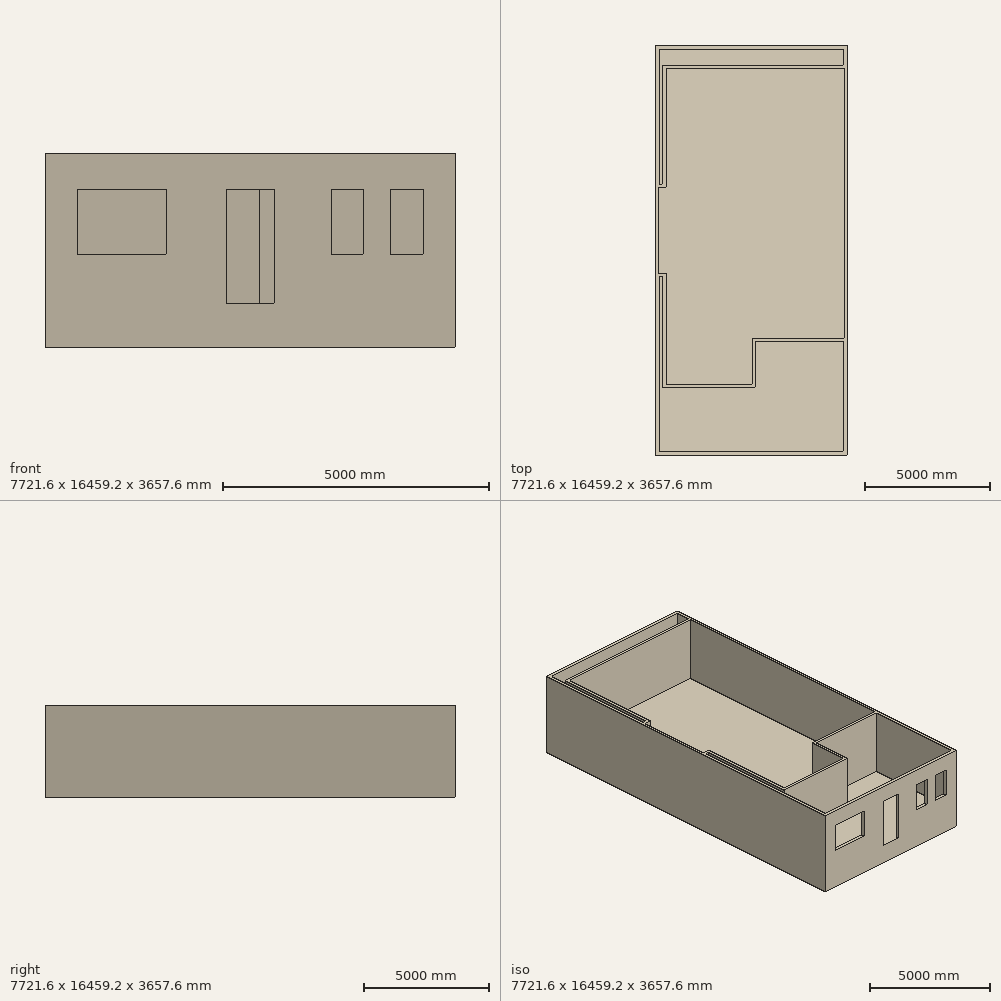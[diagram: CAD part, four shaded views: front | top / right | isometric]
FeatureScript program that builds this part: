
annotation { "Feature Type Name" : "Feature", "Feature Type Description" : "" }
export const myFeature = defineFeature(function(context is Context, id is Id, definition is map)
    precondition{}
    {
        {
            var Q0;
            Q0=qCreatedBy(makeId("Top.planeOp"),FACE);
            var sketch = newSketch(context, id + "F0", { "sketchPlane" : qUnion([Q0])});
            skLineSegment(sketch, "E0", {"start": v(3683, 0) * mm, "end": v(3683, 11099.8) * mm});
            skLineSegment(sketch, "E1", {"start": v(3683, 11099.8) * mm, "end": v(-3733.8, 11099.8) * mm});
            skLineSegment(sketch, "E2", {"start": v(-3733.8, 11099.8) * mm, "end": v(-3733.8, 6324.6) * mm});
            skLineSegment(sketch, "E3", {"start": v(-3733.8, 6324.6) * mm, "end": v(-4038.6, 6324.6) * mm});
            skLineSegment(sketch, "E4", {"start": v(-4038.6, 6324.6) * mm, "end": v(-4038.6, 2616.2) * mm});
            skLineSegment(sketch, "E5", {"start": v(-4038.6, 2616.2) * mm, "end": v(-3733.8, 2616.2) * mm});
            skLineSegment(sketch, "E6", {"start": v(-3733.8, 2616.2) * mm, "end": v(-3733.8, -1828.8) * mm});
            skLineSegment(sketch, "E7", {"start": v(0, -1828.8) * mm, "end": v(0, 0) * mm});
            skLineSegment(sketch, "E8", {"start": v(0, 0) * mm, "end": v(3683, 0) * mm});
            skPoint(sketch, "E9.orphan", {"position": v(3683, 0) * mm});
            skLineSegment(sketch, "E10", {"start": v(-3733.8, -1828.8) * mm, "end": v(0, -1828.8) * mm});
            skLineSegment(sketch, "E11.0", {"start": v(-127, -1701.8) * mm, "end": v(-127, 127) * mm});
            skLineSegment(sketch, "E11.1", {"start": v(-3606.8, -1701.8) * mm, "end": v(-127, -1701.8) * mm});
            skLineSegment(sketch, "E11.2", {"start": v(-3606.8, 2743.2) * mm, "end": v(-3606.8, -1701.8) * mm});
            skLineSegment(sketch, "E11.3", {"start": v(-3911.6, 2743.2) * mm, "end": v(-3606.8, 2743.2) * mm});
            skLineSegment(sketch, "E11.4", {"start": v(-3911.6, 6197.6) * mm, "end": v(-3911.6, 2743.2) * mm});
            skLineSegment(sketch, "E11.5", {"start": v(-127, 127) * mm, "end": v(3556, 127) * mm});
            skLineSegment(sketch, "E11.6", {"start": v(-3606.8, 6197.6) * mm, "end": v(-3911.6, 6197.6) * mm});
            skLineSegment(sketch, "E11.7", {"start": v(-3606.8, 10972.8) * mm, "end": v(-3606.8, 6197.6) * mm});
            skLineSegment(sketch, "E11.8", {"start": v(3556, 10972.8) * mm, "end": v(-3606.8, 10972.8) * mm});
            skLineSegment(sketch, "E11.9", {"start": v(3556, 127) * mm, "end": v(3556, 10972.8) * mm});
            skLineSegment(sketch, "E12.bottom", {"start": v(-3746.5, 438.15) * mm, "end": v(-3594.1, 438.15) * mm, "construction": true});
            skLineSegment(sketch, "E12.top", {"start": v(-3746.5, 1352.55) * mm, "end": v(-3594.1, 1352.55) * mm, "construction": true});
            skLineSegment(sketch, "E12.left", {"start": v(-3746.5, 438.15) * mm, "end": v(-3746.5, 1352.55) * mm, "construction": true});
            skLineSegment(sketch, "E12.right", {"start": v(-3594.1, 438.15) * mm, "end": v(-3594.1, 1352.55) * mm, "construction": true});
            skLineSegment(sketch, "E13", {"start": v(-3606.8, 2609.85) * mm, "end": v(-2933.7, 2609.85) * mm, "construction": true});
            skLineSegment(sketch, "E14", {"start": v(-2933.7, 2609.85) * mm, "end": v(-2933.7, 2743.2) * mm, "construction": true});
            skLineSegment(sketch, "E15", {"start": v(-2933.7, 2743.2) * mm, "end": v(-3606.8, 2743.2) * mm, "construction": true});
            skLineSegment(sketch, "E16.bottom", {"start": v(-2705.1, -1689.1) * mm, "end": v(-1054.1, -1689.1) * mm, "construction": true});
            skLineSegment(sketch, "E16.top", {"start": v(-2705.1, -1841.5) * mm, "end": v(-1054.1, -1841.5) * mm, "construction": true});
            skLineSegment(sketch, "E16.left", {"start": v(-2705.1, -1689.1) * mm, "end": v(-2705.1, -1841.5) * mm, "construction": true});
            skLineSegment(sketch, "E16.right", {"start": v(-1054.1, -1689.1) * mm, "end": v(-1054.1, -1841.5) * mm, "construction": true});
            skLineSegment(sketch, "E17", {"start": v(-127, 127) * mm, "end": v(-127, 2609.85) * mm, "construction": true});
            skLineSegment(sketch, "E18", {"start": v(-127, 2609.85) * mm, "end": v(-800.1, 2609.85) * mm, "construction": true});
            skLineSegment(sketch, "E19", {"start": v(-800.1, 2743.2) * mm, "end": v(-88.9, 2743.2) * mm, "construction": true});
            skLineSegment(sketch, "E20", {"start": v(-88.9, 2743.2) * mm, "end": v(660.4, 3359.05) * mm, "construction": true});
            skLineSegment(sketch, "E21", {"start": v(660.4, 3359.05) * mm, "end": v(660.4, 5268.85) * mm, "construction": true});
            skLineSegment(sketch, "E22", {"start": v(0, 127) * mm, "end": v(0, 2680.36) * mm, "construction": true});
            skLineSegment(sketch, "E23", {"start": v(76.33, 2747.5) * mm, "end": v(800.1, 1866.9) * mm, "construction": true});
            skLineSegment(sketch, "E24", {"start": v(800.1, 1866.9) * mm, "end": v(800.1, 127) * mm, "construction": true});
            skLineSegment(sketch, "E25", {"start": v(-800.1, 2743.2) * mm, "end": v(-800.1, 2609.85) * mm});
            skLineSegment(sketch, "E26", {"start": v(76.33, 2747.5) * mm, "end": v(812.8, 3352.8) * mm, "construction": true});
            skLineSegment(sketch, "E27", {"start": v(812.8, 3352.8) * mm, "end": v(3556, 3352.8) * mm, "construction": true});
            skLineSegment(sketch, "E28", {"start": v(3556, 3479.8) * mm, "end": v(787.4, 3479.8) * mm, "construction": true});
            skLineSegment(sketch, "E29", {"start": v(787.4, 3479.8) * mm, "end": v(787.4, 5181.6) * mm, "construction": true});
            skLineSegment(sketch, "E30", {"start": v(787.4, 5181.6) * mm, "end": v(3556, 5181.6) * mm, "construction": true});
            skLineSegment(sketch, "E31", {"start": v(3541.89, 5308.6) * mm, "end": v(781.97, 5308.6) * mm, "construction": true});
            skLineSegment(sketch, "E32", {"start": v(781.97, 5308.6) * mm, "end": v(0, 5845.85) * mm, "construction": true});
            skLineSegment(sketch, "E33", {"start": v(0, 8534.4) * mm, "end": v(698.5, 8534.4) * mm, "construction": true});
            skLineSegment(sketch, "E34", {"start": v(660.4, 5268.85) * mm, "end": v(-293.97, 5924.55) * mm, "construction": true});
            skLineSegment(sketch, "E35", {"start": v(-293.97, 5924.55) * mm, "end": v(-293.97, 6197.6) * mm, "construction": true});
            skLineSegment(sketch, "E36", {"start": v(-293.97, 6197.6) * mm, "end": v(-3606.8, 6197.6) * mm, "construction": true});
            skLineSegment(sketch, "E37.bottom", {"start": v(1346.2, 139.7) * mm, "end": v(2070.1, 139.7) * mm, "construction": true});
            skLineSegment(sketch, "E37.top", {"start": v(1346.2, -12.7) * mm, "end": v(2070.1, -12.7) * mm, "construction": true});
            skLineSegment(sketch, "E37.left", {"start": v(1346.2, 139.7) * mm, "end": v(1346.2, -12.7) * mm, "construction": true});
            skLineSegment(sketch, "E37.right", {"start": v(2070.1, 139.7) * mm, "end": v(2070.1, -12.7) * mm, "construction": true});
            skLineSegment(sketch, "E38.bottom", {"start": v(3543.3, 2781.3) * mm, "end": v(3695.7, 2781.3) * mm, "construction": true});
            skLineSegment(sketch, "E38.top", {"start": v(3543.3, 2051.05) * mm, "end": v(3695.7, 2051.05) * mm, "construction": true});
            skLineSegment(sketch, "E38.left", {"start": v(3543.3, 2781.3) * mm, "end": v(3543.3, 2051.05) * mm, "construction": true});
            skLineSegment(sketch, "E38.right", {"start": v(3695.7, 2781.3) * mm, "end": v(3695.7, 2051.05) * mm, "construction": true});
            skLineSegment(sketch, "E39", {"start": v(0, 2680.36) * mm, "end": v(698.5, 1830.5) * mm, "construction": true});
            skLineSegment(sketch, "E40", {"start": v(698.5, 1830.5) * mm, "end": v(698.5, 127) * mm, "construction": true});
            skLineSegment(sketch, "E41.bottom", {"start": v(3543.3, 4610.1) * mm, "end": v(3695.7, 4610.1) * mm, "construction": true});
            skLineSegment(sketch, "E41.top", {"start": v(3543.3, 4038.6) * mm, "end": v(3695.7, 4038.6) * mm, "construction": true});
            skLineSegment(sketch, "E41.left", {"start": v(3543.3, 4610.1) * mm, "end": v(3543.3, 4038.6) * mm, "construction": true});
            skLineSegment(sketch, "E41.right", {"start": v(3695.7, 4610.1) * mm, "end": v(3695.7, 4038.6) * mm, "construction": true});
            skLineSegment(sketch, "E42.bottom", {"start": v(635, 4394.2) * mm, "end": v(787.4, 4394.2) * mm, "construction": true});
            skLineSegment(sketch, "E42.top", {"start": v(635, 3632.2) * mm, "end": v(787.4, 3632.2) * mm, "construction": true});
            skLineSegment(sketch, "E42.left", {"start": v(635, 4394.2) * mm, "end": v(635, 3632.2) * mm, "construction": true});
            skLineSegment(sketch, "E42.right", {"start": v(787.4, 4394.2) * mm, "end": v(787.4, 3632.2) * mm, "construction": true});
            skLineSegment(sketch, "E43.bottom", {"start": v(-427.32, 6172.2) * mm, "end": v(-1189.32, 6172.2) * mm, "construction": true});
            skLineSegment(sketch, "E43.top", {"start": v(-427.32, 6324.6) * mm, "end": v(-1189.32, 6324.6) * mm, "construction": true});
            skLineSegment(sketch, "E43.left", {"start": v(-427.32, 6172.2) * mm, "end": v(-427.32, 6324.6) * mm, "construction": true});
            skLineSegment(sketch, "E43.right", {"start": v(-1189.32, 6172.2) * mm, "end": v(-1189.32, 6324.6) * mm, "construction": true});
            skLineSegment(sketch, "E44.bottom", {"start": v(-4064, 3619.5) * mm, "end": v(-3911.6, 3619.5) * mm, "construction": true});
            skLineSegment(sketch, "E44.top", {"start": v(-4064, 4349.75) * mm, "end": v(-3911.6, 4349.75) * mm, "construction": true});
            skLineSegment(sketch, "E44.left", {"start": v(-4064, 3619.5) * mm, "end": v(-4064, 4349.75) * mm, "construction": true});
            skLineSegment(sketch, "E44.right", {"start": v(-3911.6, 3619.5) * mm, "end": v(-3911.6, 4349.75) * mm, "construction": true});
            skLineSegment(sketch, "E45.bottom", {"start": v(3543.3, 5867.4) * mm, "end": v(3695.7, 5867.4) * mm, "construction": true});
            skLineSegment(sketch, "E45.top", {"start": v(3543.3, 7061.2) * mm, "end": v(3695.7, 7061.2) * mm, "construction": true});
            skLineSegment(sketch, "E45.left", {"start": v(3543.3, 5867.4) * mm, "end": v(3543.3, 7061.2) * mm, "construction": true});
            skLineSegment(sketch, "E45.right", {"start": v(3695.7, 5867.4) * mm, "end": v(3695.7, 7061.2) * mm, "construction": true});
            skLineSegment(sketch, "E46.bottom", {"start": v(3543.3, 9438.28) * mm, "end": v(3695.7, 9438.28) * mm, "construction": true});
            skLineSegment(sketch, "E46.top", {"start": v(3543.3, 10256.66) * mm, "end": v(3695.7, 10256.66) * mm, "construction": true});
            skLineSegment(sketch, "E46.left", {"start": v(3543.3, 9438.28) * mm, "end": v(3543.3, 10256.66) * mm, "construction": true});
            skLineSegment(sketch, "E46.right", {"start": v(3695.7, 9438.28) * mm, "end": v(3695.7, 10256.66) * mm, "construction": true});
            skLineSegment(sketch, "E47.bottom", {"start": v(2881.46, 10778.72) * mm, "end": v(1984.95, 10778.72) * mm, "construction": true});
            skLineSegment(sketch, "E47.top", {"start": v(2881.46, 10931.12) * mm, "end": v(1984.95, 10931.12) * mm, "construction": true});
            skLineSegment(sketch, "E47.left", {"start": v(2881.46, 10778.72) * mm, "end": v(2881.46, 10931.12) * mm, "construction": true});
            skLineSegment(sketch, "E47.right", {"start": v(1984.95, 10778.72) * mm, "end": v(1984.95, 10931.12) * mm, "construction": true});
            skLineSegment(sketch, "E48.bottom", {"start": v(1766.71, 10778.72) * mm, "end": v(966.52, 10778.72) * mm, "construction": true});
            skLineSegment(sketch, "E48.top", {"start": v(1766.71, 10931.12) * mm, "end": v(966.52, 10931.12) * mm, "construction": true});
            skLineSegment(sketch, "E48.left", {"start": v(1766.71, 10778.72) * mm, "end": v(1766.71, 10931.12) * mm, "construction": true});
            skLineSegment(sketch, "E48.right", {"start": v(966.52, 10778.72) * mm, "end": v(966.52, 10931.12) * mm, "construction": true});
            skLineSegment(sketch, "E49.bottom", {"start": v(-1415.88, 10778.72) * mm, "end": v(-2525.25, 10778.72) * mm, "construction": true});
            skLineSegment(sketch, "E49.top", {"start": v(-1415.88, 10931.12) * mm, "end": v(-2525.25, 10931.12) * mm, "construction": true});
            skLineSegment(sketch, "E49.left", {"start": v(-1415.88, 10778.72) * mm, "end": v(-1415.88, 10931.12) * mm, "construction": true});
            skLineSegment(sketch, "E49.right", {"start": v(-2525.25, 10778.72) * mm, "end": v(-2525.25, 10931.12) * mm, "construction": true});
            skPoint(sketch, "E50.oppositeSnap0", {"position": v(-3606.8, 8585.2) * mm});
            skLineSegment(sketch, "E50.bottom", {"start": v(-3936.87, 7828.6) * mm, "end": v(-4089.27, 7828.6) * mm, "construction": true});
            skLineSegment(sketch, "E50.top", {"start": v(-3936.87, 8585.2) * mm, "end": v(-4089.27, 8585.2) * mm, "construction": true});
            skLineSegment(sketch, "E50.left", {"start": v(-3936.87, 7828.6) * mm, "end": v(-3936.87, 8585.2) * mm, "construction": true});
            skLineSegment(sketch, "E50.right", {"start": v(-4089.27, 7828.6) * mm, "end": v(-4089.27, 8585.2) * mm, "construction": true});
            skLineSegment(sketch, "E51", {"start": v(-3606.8, 6299.2) * mm, "end": v(-293.97, 6299.2) * mm, "construction": true});
            skLineSegment(sketch, "E52", {"start": v(-293.97, 6299.2) * mm, "end": v(-293.97, 9093.2) * mm, "construction": true});
            skLineSegment(sketch, "E53", {"start": v(-293.97, 9093.2) * mm, "end": v(-805.07, 9093.2) * mm, "construction": true});
            skLineSegment(sketch, "E54", {"start": v(-805.07, 9093.2) * mm, "end": v(-805.07, 9245.6) * mm, "construction": true});
            skLineSegment(sketch, "E55", {"start": v(-805.07, 9245.6) * mm, "end": v(-293.97, 9245.6) * mm, "construction": true});
            skLineSegment(sketch, "E56", {"start": v(-293.97, 9245.6) * mm, "end": v(-293.97, 10972.8) * mm, "construction": true});
            skLineSegment(sketch, "E57", {"start": v(-107.65, 5765.72) * mm, "end": v(520.4, 5334.22) * mm, "construction": true});
            skLineSegment(sketch, "E58", {"start": v(520.4, 5334.22) * mm, "end": v(606.7, 5459.83) * mm, "construction": true});
            skLineSegment(sketch, "E59", {"start": v(606.7, 5459.83) * mm, "end": v(-21.35, 5891.33) * mm, "construction": true});
            skLineSegment(sketch, "E60", {"start": v(-21.35, 5891.33) * mm, "end": v(-107.65, 5765.72) * mm, "construction": true});
            skLineSegment(sketch, "E61", {"start": v(50.34, 2893.8) * mm, "end": v(639.02, 3377.65) * mm, "construction": true});
            skLineSegment(sketch, "E62", {"start": v(639.02, 3377.65) * mm, "end": v(735.79, 3259.91) * mm, "construction": true});
            skLineSegment(sketch, "E63", {"start": v(735.79, 3259.91) * mm, "end": v(147.1, 2776.07) * mm, "construction": true});
            skLineSegment(sketch, "E64", {"start": v(147.1, 2776.07) * mm, "end": v(50.34, 2893.8) * mm, "construction": true});
            skLineSegment(sketch, "E65", {"start": v(800.1, 8534.4) * mm, "end": v(800.1, 7010.4) * mm, "construction": true});
            skLineSegment(sketch, "E66", {"start": v(800.1, 7010.4) * mm, "end": v(0, 5845.85) * mm, "construction": true});
            skLineSegment(sketch, "E67", {"start": v(0, 6025.27) * mm, "end": v(698.5, 7041.94) * mm, "construction": true});
            skLineSegment(sketch, "E68", {"start": v(698.5, 7041.94) * mm, "end": v(698.5, 8534.4) * mm, "construction": true});
            skLineSegment(sketch, "E69.bottom", {"start": v(-4064, 4527.55) * mm, "end": v(-3911.6, 4527.55) * mm, "construction": true});
            skLineSegment(sketch, "E69.top", {"start": v(-4064, 5257.8) * mm, "end": v(-3911.6, 5257.8) * mm, "construction": true});
            skLineSegment(sketch, "E69.left", {"start": v(-4064, 4527.55) * mm, "end": v(-4064, 5257.8) * mm, "construction": true});
            skLineSegment(sketch, "E69.right", {"start": v(-3911.6, 4527.55) * mm, "end": v(-3911.6, 5257.8) * mm, "construction": true});
            skLineSegment(sketch, "E70.trimOffspring", {"start": v(800.1, 8534.4) * mm, "end": v(3556, 8534.4) * mm, "construction": true});
            skLineSegment(sketch, "E71", {"start": v(0, 8686.8) * mm, "end": v(3556, 8686.8) * mm, "construction": true});
            skLineSegment(sketch, "E72.trimOffspring", {"start": v(0, 6025.27) * mm, "end": v(0, 8534.4) * mm, "construction": true});
            skLineSegment(sketch, "E73.trimOffspring", {"start": v(0, 8686.8) * mm, "end": v(0, 10972.8) * mm, "construction": true});
            skSolve(sketch);
        }
        {
            var Q0;
            Q0 = qSketchRegion(id + "F0", true);
            extrude(context, id + "F1", {"entities" : qUnion([Q0]), "depth" : 3657.6 * mm});
        }
        {
            var Q0;
            Q0=qCreatedBy(makeId("Top.planeOp"),FACE);
            var sketch = newSketch(context, id + "F2", { "sketchPlane" : qUnion([Q0])});
            skLineSegment(sketch, "E74.bottom", {"start": v(3683, -4572) * mm, "end": v(-4038.6, -4572) * mm});
            skLineSegment(sketch, "E74.top", {"start": v(3683, 11887.2) * mm, "end": v(-4038.6, 11887.2) * mm});
            skLineSegment(sketch, "E74.left", {"start": v(3683, -4572) * mm, "end": v(3683, 0) * mm});
            skLineSegment(sketch, "E74.right", {"start": v(-4038.6, -4572) * mm, "end": v(-4038.6, 2616.2) * mm});
            skLineSegment(sketch, "E75.0", {"start": v(3530.6, 11734.8) * mm, "end": v(-3886.2, 11734.8) * mm});
            skLineSegment(sketch, "E75.1", {"start": v(-3886.2, -4419.6) * mm, "end": v(-3886.2, 2616.2) * mm});
            skLineSegment(sketch, "E75.2", {"start": v(3530.6, -4419.6) * mm, "end": v(-3886.2, -4419.6) * mm});
            skLineSegment(sketch, "E75.3", {"start": v(3530.6, -4419.6) * mm, "end": v(3530.6, 0) * mm});
            skLineSegment(sketch, "E76", {"start": v(3530.6, 0) * mm, "end": v(3683, 0) * mm});
            skLineSegment(sketch, "E77", {"start": v(-4038.6, 2616.2) * mm, "end": v(-3886.2, 2616.2) * mm});
            skLineSegment(sketch, "E78", {"start": v(-4038.6, 6324.6) * mm, "end": v(-3886.2, 6324.6) * mm});
            skLineSegment(sketch, "E79.trimOffspring", {"start": v(-3886.2, 6324.6) * mm, "end": v(-3886.2, 11734.8) * mm});
            skLineSegment(sketch, "E80.trimOffspring", {"start": v(-4038.6, 6324.6) * mm, "end": v(-4038.6, 11887.2) * mm});
            skLineSegment(sketch, "E81", {"start": v(3683, 11887.2) * mm, "end": v(3683, 11099.8) * mm});
            skLineSegment(sketch, "E82", {"start": v(3683, 11099.8) * mm, "end": v(3530.6, 11099.8) * mm});
            skLineSegment(sketch, "E83", {"start": v(3530.6, 11099.8) * mm, "end": v(3530.6, 11734.8) * mm});
            skSolve(sketch);
        }
        {
            var Q0;
            Q0 = qSketchRegion(id + "F2", true);
            extrude(context, id + "F3", {"entities" : qUnion([Q0]), "operationType" : NewBodyOperationType.ADD, "depth" : 762 * mm});
        }
        {
            var Q0;
            Q0=makeQuery(id+"F3.opExtrude","CAP_FACE",FACE,{"disambiguationData":[OSD([sQuery(id+"F2.wireOp",EDGE,"E74.bottom"),sQuery(id+"F2.wireOp",EDGE,"E74.left"),sQuery(id+"F2.wireOp",EDGE,"E74.right"),sQuery(id+"F2.wireOp",EDGE,"E75.1"),sQuery(id+"F2.wireOp",EDGE,"E75.2"),sQuery(id+"F2.wireOp",EDGE,"E75.3"),sQuery(id+"F2.wireOp",EDGE,"E76"),sQuery(id+"F2.wireOp",EDGE,"E77")])],"isStart":false});
            var sketch = newSketch(context, id + "F4", { "sketchPlane" : qUnion([Q0])});
            skLineSegment(sketch, "E84.0", {"start": v(3683, -4572) * mm, "end": v(3683, 0) * mm});
            skLineSegment(sketch, "E85.0", {"start": v(3683, -4572) * mm, "end": v(-4038.6, -4572) * mm});
            skLineSegment(sketch, "E86.1", {"start": v(-4038.6, -4572) * mm, "end": v(-4038.6, 2616.2) * mm});
            skLineSegment(sketch, "E87.2", {"start": v(-4038.6, 6324.6) * mm, "end": v(-4038.6, 2616.2) * mm});
            skLineSegment(sketch, "E88.3", {"start": v(-4038.6, 6324.6) * mm, "end": v(-4038.6, 11887.2) * mm});
            skLineSegment(sketch, "E89.4", {"start": v(3683, 11887.2) * mm, "end": v(-4038.6, 11887.2) * mm});
            skLineSegment(sketch, "E89.5", {"start": v(3683, 0) * mm, "end": v(3683, 11099.8) * mm});
            skLineSegment(sketch, "E90.0", {"start": v(3683, 11887.2) * mm, "end": v(3683, 11099.8) * mm});
            skSolve(sketch);
        }
        {
            var Q0;
            Q0 = qSketchRegion(id + "F4", true);
            extrude(context, id + "F5", {"entities" : qUnion([Q0]), "operationType" : NewBodyOperationType.ADD, "depth" : 76.2 * mm});
        }
        {
            var Q0;
            {var subQ0=sQuery(id+"F4.wireOp",EDGE,"E84.0");var subQ1=sQuery(id+"F4.wireOp",EDGE,"E85.0");var subQ2=sQuery(id+"F4.wireOp",EDGE,"E86.1");var subQ3=sQuery(id+"F4.wireOp",EDGE,"E87.2");var subQ4=sQuery(id+"F4.wireOp",EDGE,"E88.3");var subQ5=sQuery(id+"F4.wireOp",EDGE,"E89.5");var subQ6=sQuery(id+"F4.wireOp",EDGE,"E90.0");Q0=makeQuery(id+"F5.boolean.opBoolean","SPLIT",FACE,{"disambiguationData":[TD([makeQuery(id+"F1.opExtrude","SWEPT_FACE",FACE,{"disambiguationData":[OSD([sQuery(id+"F0.wireOp",EDGE,"E5")])]})])],"derivedFrom":makeQuery(id+"F5.opExtrude","CAP_FACE",FACE,{"disambiguationData":[OSD([subQ0,subQ1,subQ2,subQ3,subQ4,sQuery(id+"F4.wireOp",EDGE,"E89.4"),subQ5,subQ6])],"isStart":false})});}
            var sketch = newSketch(context, id + "F6", { "sketchPlane" : qUnion([Q0])});
            skLineSegment(sketch, "E91.0", {"start": v(3683, -4572) * mm, "end": v(-4038.6, -4572) * mm});
            skLineSegment(sketch, "E91.1", {"start": v(3683, 11887.2) * mm, "end": v(-4038.6, 11887.2) * mm});
            skLineSegment(sketch, "E91.2", {"start": v(3683, -4572) * mm, "end": v(3683, 0) * mm});
            skLineSegment(sketch, "E91.3", {"start": v(-4038.6, -4572) * mm, "end": v(-4038.6, 2616.2) * mm});
            skLineSegment(sketch, "E91.4", {"start": v(3530.6, 11734.8) * mm, "end": v(-3886.2, 11734.8) * mm});
            skLineSegment(sketch, "E91.5", {"start": v(-3886.2, -4419.6) * mm, "end": v(-3886.2, 2616.2) * mm});
            skLineSegment(sketch, "E91.6", {"start": v(3530.6, -4419.6) * mm, "end": v(-3886.2, -4419.6) * mm});
            skLineSegment(sketch, "E91.7", {"start": v(3530.6, -4419.6) * mm, "end": v(3530.6, 0) * mm});
            skLineSegment(sketch, "E91.8", {"start": v(3530.6, 0) * mm, "end": v(3683, 0) * mm});
            skLineSegment(sketch, "E91.9", {"start": v(-4038.6, 2616.2) * mm, "end": v(-3886.2, 2616.2) * mm});
            skLineSegment(sketch, "E91.10", {"start": v(-4038.6, 6324.6) * mm, "end": v(-3886.2, 6324.6) * mm});
            skLineSegment(sketch, "E91.11", {"start": v(-3886.2, 6324.6) * mm, "end": v(-3886.2, 11734.8) * mm});
            skLineSegment(sketch, "E91.12", {"start": v(-4038.6, 6324.6) * mm, "end": v(-4038.6, 11887.2) * mm});
            skLineSegment(sketch, "E91.13", {"start": v(3683, 11887.2) * mm, "end": v(3683, 11099.8) * mm});
            skLineSegment(sketch, "E91.14", {"start": v(3683, 11099.8) * mm, "end": v(3530.6, 11099.8) * mm});
            skLineSegment(sketch, "E91.15", {"start": v(3530.6, 11099.8) * mm, "end": v(3530.6, 11734.8) * mm});
            skSolve(sketch);
        }
        {
            var Q0;
            Q0 = qSketchRegion(id + "F2", true);
            var Q1;
            Q1=makeQuery(id+"F1.opExtrude","CAP_FACE",FACE,{"disambiguationData":[OSD([sQuery(id+"F0.wireOp",EDGE,"E0"),sQuery(id+"F0.wireOp",EDGE,"E1"),sQuery(id+"F0.wireOp",EDGE,"E2"),sQuery(id+"F0.wireOp",EDGE,"E3"),sQuery(id+"F0.wireOp",EDGE,"E4"),sQuery(id+"F0.wireOp",EDGE,"E5"),sQuery(id+"F0.wireOp",EDGE,"E6"),sQuery(id+"F0.wireOp",EDGE,"E7"),sQuery(id+"F0.wireOp",EDGE,"E8"),sQuery(id+"F0.wireOp",EDGE,"E10"),sQuery(id+"F0.wireOp",EDGE,"E11.0"),sQuery(id+"F0.wireOp",EDGE,"E11.1"),sQuery(id+"F0.wireOp",EDGE,"E11.2"),sQuery(id+"F0.wireOp",EDGE,"E11.3"),sQuery(id+"F0.wireOp",EDGE,"E11.4"),sQuery(id+"F0.wireOp",EDGE,"E11.5"),sQuery(id+"F0.wireOp",EDGE,"E11.6"),sQuery(id+"F0.wireOp",EDGE,"E11.7"),sQuery(id+"F0.wireOp",EDGE,"E11.8"),sQuery(id+"F0.wireOp",EDGE,"E11.9")])],"isStart":false});
            extrude(context, id + "F7", {"entities" : qUnion([Q0]), "operationType" : NewBodyOperationType.ADD, "endBound" : BoundingType.UP_TO_SURFACE, "endBoundEntityFace" : qUnion([Q1]), "depth" : 25.4 * mm});
        }
        {
            var Q0;
            {var subQ0=sQuery(id+"F2.wireOp",EDGE,"E74.bottom");Q0=makeQuery(id+"F7.boolean.opBoolean","MERGE",FACE,{"derivedFrom":[makeQuery(id+"F5.boolean.opBoolean","MERGE",FACE,{"derivedFrom":[makeQuery(id+"F3.opExtrude","SWEPT_FACE",FACE,{"disambiguationData":[OSD([subQ0])]}),makeQuery(id+"F5.opExtrude","SWEPT_FACE",FACE,{"disambiguationData":[OSD([sQuery(id+"F4.wireOp",EDGE,"E85.0")])]})]}),makeQuery(id+"F7.opExtrude","SWEPT_FACE",FACE,{"disambiguationData":[OSD([subQ0])]})]});}
            var sketch = newSketch(context, id + "F8", { "sketchPlane" : qUnion([Q0])});
            skLineSegment(sketch, "E92.bottom", {"start": v(-3429, 2971.8) * mm, "end": v(-1752.6, 2971.8) * mm});
            skLineSegment(sketch, "E92.top", {"start": v(-3429, 1752.6) * mm, "end": v(-1752.6, 1752.6) * mm});
            skLineSegment(sketch, "E92.left", {"start": v(-3429, 2971.8) * mm, "end": v(-3429, 1752.6) * mm});
            skLineSegment(sketch, "E92.right", {"start": v(-1752.6, 2971.8) * mm, "end": v(-1752.6, 1752.6) * mm});
            skLineSegment(sketch, "E93.bottom", {"start": v(-635, 838.2) * mm, "end": v(279.4, 838.2) * mm});
            skLineSegment(sketch, "E93.top", {"start": v(-635, 2971.8) * mm, "end": v(279.4, 2971.8) * mm});
            skLineSegment(sketch, "E93.left", {"start": v(-635, 838.2) * mm, "end": v(-635, 2971.8) * mm});
            skLineSegment(sketch, "E93.right", {"start": v(279.4, 838.2) * mm, "end": v(279.4, 2971.8) * mm});
            skLineSegment(sketch, "E94.bottom", {"start": v(2463.8, 2971.8) * mm, "end": v(3073.4, 2971.8) * mm});
            skLineSegment(sketch, "E94.top", {"start": v(2463.8, 1752.6) * mm, "end": v(3073.4, 1752.6) * mm});
            skLineSegment(sketch, "E94.left", {"start": v(2463.8, 2971.8) * mm, "end": v(2463.8, 1752.6) * mm});
            skLineSegment(sketch, "E94.right", {"start": v(3073.4, 2971.8) * mm, "end": v(3073.4, 1752.6) * mm});
            skLineSegment(sketch, "E95.bottom", {"start": v(1346.2, 1752.6) * mm, "end": v(1955.8, 1752.6) * mm});
            skLineSegment(sketch, "E95.top", {"start": v(1346.2, 2971.8) * mm, "end": v(1955.8, 2971.8) * mm});
            skLineSegment(sketch, "E95.left", {"start": v(1346.2, 1752.6) * mm, "end": v(1346.2, 2971.8) * mm});
            skLineSegment(sketch, "E95.right", {"start": v(1955.8, 1752.6) * mm, "end": v(1955.8, 2971.8) * mm});
            skSolve(sketch);
        }
        {
            var Q0;
            Q0 = qSketchRegion(id + "F8", true);
            extrude(context, id + "F9", {"entities" : qUnion([Q0]), "operationType" : NewBodyOperationType.REMOVE, "endBound" : BoundingType.UP_TO_NEXT, "oppositeDirection" : true, "depth" : 25.4 * mm});
        }
    });
